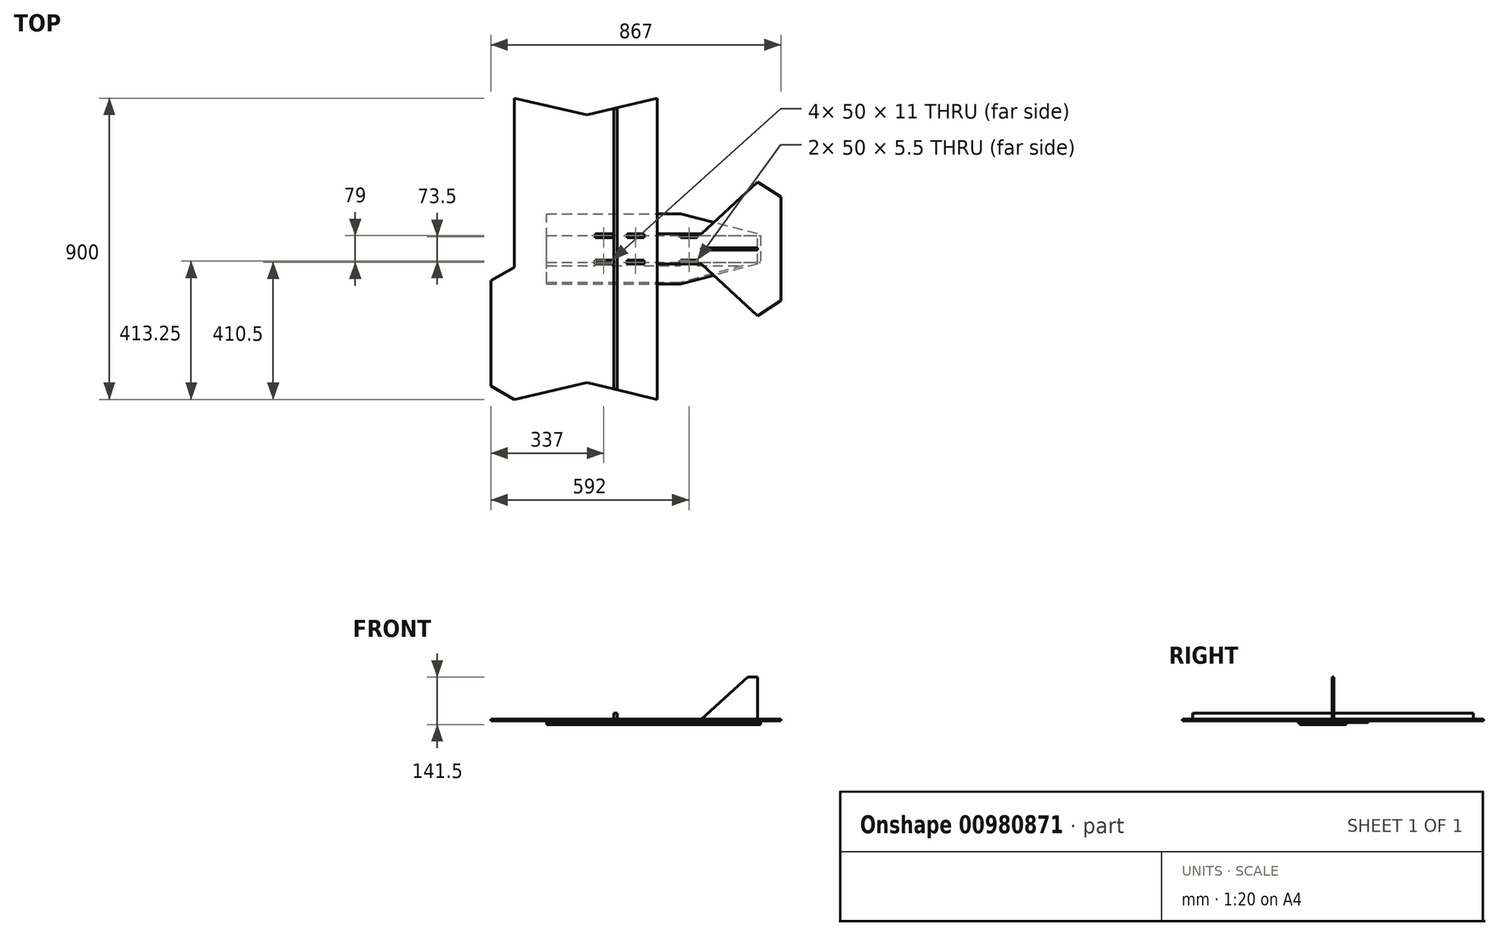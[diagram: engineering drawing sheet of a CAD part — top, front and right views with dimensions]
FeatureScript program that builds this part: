
annotation { "Feature Type Name" : "Feature", "Feature Type Description" : "" }
export const myFeature = defineFeature(function(context is Context, id is Id, definition is map)
    precondition{}
    {
        {
            var Q0;
            Q0=qCreatedBy(makeId("Top.planeOp"),FACE);
            var sketch = newSketch(context, id + "F0", { "sketchPlane" : qUnion([Q0])});
            skPoint(sketch, "E0.middle", {"position": v(0, 0) * mm});
            skLineSegment(sketch, "E1.bottom", {"start": v(0, 0) * mm, "end": v(-287, 0) * mm, "construction": true});
            skLineSegment(sketch, "E1.left", {"start": v(0, 0) * mm, "end": v(0, 400) * mm});
            skLineSegment(sketch, "E2.MirrorCS", {"start": v(0, 0) * mm, "end": v(0, -400) * mm});
            skLineSegment(sketch, "E3.bottom", {"start": v(0, 0) * mm, "end": v(210, 0) * mm, "construction": true});
            skLineSegment(sketch, "E3.right", {"start": v(210, 0) * mm, "end": v(210, 450) * mm});
            skLineSegment(sketch, "E4.MirrorCS", {"start": v(210, 0) * mm, "end": v(210, -450) * mm});
            skLineSegment(sketch, "E5", {"start": v(-217, 450) * mm, "end": v(-217, 55) * mm});
            skLineSegment(sketch, "E6", {"start": v(0, 400) * mm, "end": v(210, 450) * mm});
            skLineSegment(sketch, "E7", {"start": v(-217, 450) * mm, "end": v(-217, 400) * mm});
            skLineSegment(sketch, "E8", {"start": v(-217, 450) * mm, "end": v(0, 400) * mm});
            skLineSegment(sketch, "E9.MirrorCS", {"start": v(-217, -450) * mm, "end": v(0, -400) * mm});
            skLineSegment(sketch, "E10.MirrorCS", {"start": v(0, -400) * mm, "end": v(210, -450) * mm});
            skLineSegment(sketch, "E11", {"start": v(210, 45) * mm, "end": v(-287, 45) * mm, "construction": true});
            skLineSegment(sketch, "E12.MirrorCS", {"start": v(25, 45) * mm, "end": v(25, 34) * mm});
            skLineSegment(sketch, "E13.MirrorCS", {"start": v(75, 45) * mm, "end": v(75, 34) * mm});
            skLineSegment(sketch, "E14.MirrorCS", {"start": v(170, 45) * mm, "end": v(170, 34) * mm});
            skLineSegment(sketch, "E15.MirrorCS", {"start": v(120, 45) * mm, "end": v(120, 34) * mm});
            skLineSegment(sketch, "E16.MirrorCS", {"start": v(25, 45) * mm, "end": v(75, 45) * mm});
            skLineSegment(sketch, "E17.MirrorCS", {"start": v(120, 34) * mm, "end": v(170, 34) * mm});
            skLineSegment(sketch, "E18.MirrorCS", {"start": v(25, 34) * mm, "end": v(75, 34) * mm});
            skLineSegment(sketch, "E19.MirrorCS", {"start": v(120, 45) * mm, "end": v(170, 45) * mm});
            skLineSegment(sketch, "E20.MirrorCS", {"start": v(120, -45) * mm, "end": v(120, -34) * mm});
            skLineSegment(sketch, "E21.MirrorCS", {"start": v(75, -45) * mm, "end": v(75, -34) * mm});
            skLineSegment(sketch, "E22.MirrorCS", {"start": v(25, -45) * mm, "end": v(25, -34) * mm});
            skLineSegment(sketch, "E23.MirrorCS", {"start": v(170, -45) * mm, "end": v(170, -34) * mm});
            skLineSegment(sketch, "E24.MirrorCS", {"start": v(25, -45) * mm, "end": v(75, -45) * mm});
            skLineSegment(sketch, "E25.MirrorCS", {"start": v(120, -45) * mm, "end": v(170, -45) * mm});
            skLineSegment(sketch, "E26.MirrorCS", {"start": v(210, -45) * mm, "end": v(-287, -45) * mm, "construction": true});
            skLineSegment(sketch, "E27.MirrorCS", {"start": v(120, -34) * mm, "end": v(170, -34) * mm});
            skLineSegment(sketch, "E28.MirrorCS", {"start": v(25, -34) * mm, "end": v(75, -34) * mm});
            skLineSegment(sketch, "E29", {"start": v(80, 450) * mm, "end": v(80, -450) * mm, "construction": true});
            skLineSegment(sketch, "E30.bottom", {"start": v(80, 115) * mm, "end": v(91, 115) * mm});
            skLineSegment(sketch, "E30.top", {"start": v(80, 165) * mm, "end": v(91, 165) * mm});
            skLineSegment(sketch, "E30.left", {"start": v(80, 115) * mm, "end": v(80, 165) * mm});
            skLineSegment(sketch, "E30.right", {"start": v(91, 115) * mm, "end": v(91, 165) * mm});
            skLineSegment(sketch, "E31.bottom", {"start": v(80, 275) * mm, "end": v(91, 275) * mm});
            skLineSegment(sketch, "E31.top", {"start": v(80, 325) * mm, "end": v(91, 325) * mm});
            skLineSegment(sketch, "E31.left", {"start": v(80, 275) * mm, "end": v(80, 325) * mm});
            skLineSegment(sketch, "E31.right", {"start": v(91, 275) * mm, "end": v(91, 325) * mm});
            skLineSegment(sketch, "E32.MirrorCS", {"start": v(80, -275) * mm, "end": v(80, -325) * mm});
            skLineSegment(sketch, "E33.MirrorCS", {"start": v(80, -115) * mm, "end": v(80, -165) * mm});
            skLineSegment(sketch, "E34.MirrorCS", {"start": v(91, -115) * mm, "end": v(91, -165) * mm});
            skLineSegment(sketch, "E35.MirrorCS", {"start": v(91, -275) * mm, "end": v(91, -325) * mm});
            skLineSegment(sketch, "E36.MirrorCS", {"start": v(80, -165) * mm, "end": v(91, -165) * mm});
            skLineSegment(sketch, "E37.MirrorCS", {"start": v(80, -325) * mm, "end": v(91, -325) * mm});
            skLineSegment(sketch, "E38.MirrorCS", {"start": v(80, -450) * mm, "end": v(80, 419.05) * mm, "construction": true});
            skLineSegment(sketch, "E39.MirrorCS", {"start": v(80, -115) * mm, "end": v(91, -115) * mm});
            skLineSegment(sketch, "E40.MirrorCS", {"start": v(80, -275) * mm, "end": v(91, -275) * mm});
            skLineSegment(sketch, "E41", {"start": v(-217, -450) * mm, "end": v(-287, -410) * mm});
            skLineSegment(sketch, "E42.MirrorCS", {"start": v(-217, 450) * mm, "end": v(-287, 410) * mm});
            skLineSegment(sketch, "E43", {"start": v(-287, -85) * mm, "end": v(-287, -85) * mm});
            skLineSegment(sketch, "E44", {"start": v(-287, 95) * mm, "end": v(-287, 410) * mm});
            skPoint(sketch, "E45.orphan", {"position": v(-287, -450) * mm});
            skLineSegment(sketch, "E46.trimOffspring", {"start": v(-287, -95) * mm, "end": v(-287, -410) * mm});
            skPoint(sketch, "E47.MirrorCS.start.orphan", {"position": v(-287, 0) * mm});
            skPoint(sketch, "E48.end.orphan", {"position": v(-287, 450) * mm});
            skPoint(sketch, "E49.orphan", {"position": v(0, 450) * mm});
            skPoint(sketch, "E50.orphan", {"position": v(80, 450) * mm});
            skPoint(sketch, "E51.MirrorCS.start.orphan", {"position": v(0, -450) * mm});
            skPoint(sketch, "E52.MirrorCS.end.orphan", {"position": v(210, -450) * mm});
            skLineSegment(sketch, "E53", {"start": v(-217, 55) * mm, "end": v(-144.76, 55) * mm, "construction": true});
            skLineSegment(sketch, "E54", {"start": v(-287, 95) * mm, "end": v(-242.26, 95) * mm, "construction": true});
            skLineSegment(sketch, "E55", {"start": v(-287, 95) * mm, "end": v(-217, 55) * mm});
            skPoint(sketch, "E56.MirrorCS.end.orphan", {"position": v(-287, 85) * mm});
            skLineSegment(sketch, "E57.MirrorCS", {"start": v(-287, -95) * mm, "end": v(-217, -55) * mm});
            skLineSegment(sketch, "E58.trimOffspring", {"start": v(-217, -55) * mm, "end": v(-217, -450) * mm});
            skPoint(sketch, "E59.trimOffspring.end.orphan", {"position": v(-217, -45) * mm});
            skPoint(sketch, "E60.start.orphan", {"position": v(-217, 45) * mm});
            skLineSegment(sketch, "E61", {"start": v(-217, 55) * mm, "end": v(-217, -55) * mm});
            skSolve(sketch);
        }
        {
            var Q0;
            {var subQ4=sQuery(id+"F0.wireOp",EDGE,"E1.left");Q0=makeQuery(id+"F0.imprint","IMPRINT",FACE,{"disambiguationData":[TD([[makeQuery(id+"F0.imprint","IMPRINT",EDGE,{"derivedFrom":subQ4}),1.0]])]});}
            var Q1;
            {var subQ1=sQuery(id+"F0.wireOp",EDGE,"E7");Q1=makeQuery(id+"F0.imprint","IMPRINT",FACE,{"disambiguationData":[TD([[makeQuery(id+"F0.imprint","IMPRINT",EDGE,{"derivedFrom":subQ1}),-1.0]])]});}
            var Q2;
            {var subQ0=sQuery(id+"F0.wireOp",EDGE,"lml2tlPo-69tN-Frwz-FPkp-IQI1zHHmHSO9");Q2=makeQuery(id+"F0.imprint","IMPRINT",FACE,{"disambiguationData":[TD([[makeQuery(id+"F0.imprint","IMPRINT",EDGE,{"derivedFrom":subQ0}),1.0]])]});}
            var Q3;
            {var subQ1=sQuery(id+"F0.wireOp",EDGE,"E1.left");Q3=makeQuery(id+"F0.imprint","IMPRINT",FACE,{"disambiguationData":[TD([[makeQuery(id+"F0.imprint","IMPRINT",EDGE,{"derivedFrom":subQ1}),-1.0]])]});}
            var Q4;
            Q4=makeQuery(id+"F0.imprint","IMPRINT",FACE,{"disambiguationData":[TD([[makeQuery(id+"F0.imprint","IMPRINT",EDGE,{"derivedFrom":sQuery(id+"F0.wireOp",EDGE,"E41")}),-1.0]])]});
            extrude(context, id + "F1", {"entities" : qUnion([Q0, Q1, Q2, Q3, Q4]), "depth" : 5.5 * mm, "offsetDistance" : 25 * mm});
        }
        {
            var Q0;
            Q0=makeQuery(id+"F1.opExtrude","CAP_FACE",FACE,{"disambiguationData":[OSD([sQuery(id+"F0.wireOp",EDGE,"E1.right"),sQuery(id+"F0.wireOp",EDGE,"E47.MirrorCS"),sQuery(id+"F0.wireOp",EDGE,"E3.right"),sQuery(id+"F0.wireOp",EDGE,"E4.MirrorCS"),sQuery(id+"F0.wireOp",EDGE,"E5"),sQuery(id+"F0.wireOp",EDGE,"E6"),sQuery(id+"F0.wireOp",EDGE,"E8"),sQuery(id+"F0.wireOp",EDGE,"E9.MirrorCS"),sQuery(id+"F0.wireOp",EDGE,"E10.MirrorCS"),sQuery(id+"F0.wireOp",EDGE,"E12.MirrorCS"),sQuery(id+"F0.wireOp",EDGE,"E13.MirrorCS"),sQuery(id+"F0.wireOp",EDGE,"E14.MirrorCS"),sQuery(id+"F0.wireOp",EDGE,"E15.MirrorCS"),sQuery(id+"F0.wireOp",EDGE,"E16.MirrorCS"),sQuery(id+"F0.wireOp",EDGE,"E17.MirrorCS"),sQuery(id+"F0.wireOp",EDGE,"E18.MirrorCS"),sQuery(id+"F0.wireOp",EDGE,"E19.MirrorCS"),sQuery(id+"F0.wireOp",EDGE,"E20.MirrorCS"),sQuery(id+"F0.wireOp",EDGE,"E21.MirrorCS"),sQuery(id+"F0.wireOp",EDGE,"E22.MirrorCS"),sQuery(id+"F0.wireOp",EDGE,"E23.MirrorCS"),sQuery(id+"F0.wireOp",EDGE,"E24.MirrorCS"),sQuery(id+"F0.wireOp",EDGE,"E25.MirrorCS"),sQuery(id+"F0.wireOp",EDGE,"E27.MirrorCS"),sQuery(id+"F0.wireOp",EDGE,"E28.MirrorCS"),sQuery(id+"F0.wireOp",EDGE,"E30.bottom"),sQuery(id+"F0.wireOp",EDGE,"E30.top"),sQuery(id+"F0.wireOp",EDGE,"E30.left"),sQuery(id+"F0.wireOp",EDGE,"E30.right"),sQuery(id+"F0.wireOp",EDGE,"E31.bottom"),sQuery(id+"F0.wireOp",EDGE,"E31.top"),sQuery(id+"F0.wireOp",EDGE,"E31.left"),sQuery(id+"F0.wireOp",EDGE,"E31.right"),sQuery(id+"F0.wireOp",EDGE,"E32.MirrorCS"),sQuery(id+"F0.wireOp",EDGE,"E33.MirrorCS"),sQuery(id+"F0.wireOp",EDGE,"E34.MirrorCS"),sQuery(id+"F0.wireOp",EDGE,"E35.MirrorCS"),sQuery(id+"F0.wireOp",EDGE,"E36.MirrorCS"),sQuery(id+"F0.wireOp",EDGE,"E37.MirrorCS"),sQuery(id+"F0.wireOp",EDGE,"E39.MirrorCS"),sQuery(id+"F0.wireOp",EDGE,"E40.MirrorCS"),sQuery(id+"F0.wireOp",EDGE,"lml2tlPo-69tN-Frwz-FPkp-IQI1zHHmHSO9"),sQuery(id+"F0.wireOp",EDGE,"E41"),sQuery(id+"F0.wireOp",EDGE,"E56.MirrorCS"),sQuery(id+"F0.wireOp",EDGE,"E42.MirrorCS")])],"isStart":false});
            var sketch = newSketch(context, id + "F2", { "sketchPlane" : qUnion([Q0])});
            skLineSegment(sketch, "E62.0", {"start": v(80, -450) * mm, "end": v(80, 419.05) * mm});
            skLineSegment(sketch, "E63.0", {"start": v(91, -275) * mm, "end": v(91, -325) * mm});
            skLineSegment(sketch, "E63.1", {"start": v(80, -275) * mm, "end": v(80, -325) * mm});
            skLineSegment(sketch, "E63.2", {"start": v(80, -115) * mm, "end": v(80, -165) * mm});
            skLineSegment(sketch, "E63.3", {"start": v(91, -115) * mm, "end": v(91, -165) * mm});
            skLineSegment(sketch, "E64.0", {"start": v(91, 115) * mm, "end": v(91, 165) * mm});
            skLineSegment(sketch, "E64.1", {"start": v(80, 115) * mm, "end": v(80, 165) * mm});
            skLineSegment(sketch, "E64.2", {"start": v(80, 275) * mm, "end": v(80, 325) * mm});
            skLineSegment(sketch, "E64.3", {"start": v(91, 275) * mm, "end": v(91, 325) * mm});
            skPoint(sketch, "E65.0", {"position": v(105, 425) * mm});
            skLineSegment(sketch, "E66.0", {"start": v(0, -400) * mm, "end": v(210, -450) * mm});
            skLineSegment(sketch, "E67.0", {"start": v(0, 400) * mm, "end": v(210, 450) * mm});
            skLineSegment(sketch, "E68", {"start": v(80, 419.05) * mm, "end": v(91, 419.05) * mm});
            skLineSegment(sketch, "E69.bottom", {"start": v(80, -419.05) * mm, "end": v(91, -419.05) * mm});
            skLineSegment(sketch, "E69.left", {"start": v(80, -419.05) * mm, "end": v(80, 419.05) * mm});
            skLineSegment(sketch, "E69.right", {"start": v(91, -419.05) * mm, "end": v(91, 419.05) * mm});
            skSolve(sketch);
        }
        {
            var Q0;
            {var subQ0=sQuery(id+"F2.wireOp",EDGE,"E69.bottom");Q0=makeQuery(id+"F2.imprint","IMPRINT",FACE,{"disambiguationData":[TD([[makeQuery(id+"F2.imprint","IMPRINT",EDGE,{"derivedFrom":subQ0}),1.0]])]});}
            var Q1;
            {var subQ2=makeQuery(id+"F1.opExtrude","CAP_EDGE",EDGE,{"disambiguationData":[OSD([sQuery(id+"F0.wireOp",EDGE,"E37.MirrorCS")])],"isStart":false});Q1=makeQuery(id+"F2.imprint","IMPRINT",FACE,{"disambiguationData":[TD([[makeQuery(id+"F2.imprint","IMPRINT",EDGE,{"derivedFrom":subQ2}),1.0]])]});}
            var Q2;
            {var subQ2=makeQuery(id+"F1.opExtrude","CAP_EDGE",EDGE,{"disambiguationData":[OSD([sQuery(id+"F0.wireOp",EDGE,"E36.MirrorCS")])],"isStart":false});Q2=makeQuery(id+"F2.imprint","IMPRINT",FACE,{"disambiguationData":[TD([[makeQuery(id+"F2.imprint","IMPRINT",EDGE,{"derivedFrom":subQ2}),-1.0]])]});}
            var Q3;
            {var subQ2=makeQuery(id+"F1.opExtrude","CAP_EDGE",EDGE,{"disambiguationData":[OSD([sQuery(id+"F0.wireOp",EDGE,"E36.MirrorCS")])],"isStart":false});Q3=makeQuery(id+"F2.imprint","IMPRINT",FACE,{"disambiguationData":[TD([[makeQuery(id+"F2.imprint","IMPRINT",EDGE,{"derivedFrom":subQ2}),1.0]])]});}
            var Q4;
            {var subQ1=makeQuery(id+"F1.opExtrude","CAP_EDGE",EDGE,{"disambiguationData":[OSD([sQuery(id+"F0.wireOp",EDGE,"E30.bottom")])],"isStart":false});Q4=makeQuery(id+"F2.imprint","IMPRINT",FACE,{"disambiguationData":[TD([[makeQuery(id+"F2.imprint","IMPRINT",EDGE,{"derivedFrom":subQ1}),-1.0]])]});}
            var Q5;
            {var subQ1=makeQuery(id+"F1.opExtrude","CAP_EDGE",EDGE,{"disambiguationData":[OSD([sQuery(id+"F0.wireOp",EDGE,"E30.bottom")])],"isStart":false});Q5=makeQuery(id+"F2.imprint","IMPRINT",FACE,{"disambiguationData":[TD([[makeQuery(id+"F2.imprint","IMPRINT",EDGE,{"derivedFrom":subQ1}),1.0]])]});}
            var Q6;
            {var subQ1=makeQuery(id+"F1.opExtrude","CAP_EDGE",EDGE,{"disambiguationData":[OSD([sQuery(id+"F0.wireOp",EDGE,"E30.top")])],"isStart":false});Q6=makeQuery(id+"F2.imprint","IMPRINT",FACE,{"disambiguationData":[TD([[makeQuery(id+"F2.imprint","IMPRINT",EDGE,{"derivedFrom":subQ1}),1.0]])]});}
            var Q7;
            {var subQ0=sQuery(id+"F2.wireOp",EDGE,"E68");Q7=makeQuery(id+"F2.imprint","IMPRINT",FACE,{"disambiguationData":[TD([[makeQuery(id+"F2.imprint","IMPRINT",EDGE,{"derivedFrom":subQ0}),-1.0]])]});}
            var Q8;
            {var subQ1=makeQuery(id+"F1.opExtrude","CAP_EDGE",EDGE,{"disambiguationData":[OSD([sQuery(id+"F0.wireOp",EDGE,"E31.bottom")])],"isStart":false});Q8=makeQuery(id+"F2.imprint","IMPRINT",FACE,{"disambiguationData":[TD([[makeQuery(id+"F2.imprint","IMPRINT",EDGE,{"derivedFrom":subQ1}),1.0]])]});}
            extrude(context, id + "F3", {"entities" : qUnion([Q0, Q1, Q2, Q3, Q4, Q5, Q6, Q7, Q8]), "depth" : 18 * mm, "offsetDistance" : 25 * mm});
        }
        {
            var Q0;
            Q0=makeQuery(id+"F0.imprint","IMPRINT",FACE,{"disambiguationData":[TD([[makeQuery(id+"F0.imprint","IMPRINT",EDGE,{"derivedFrom":sQuery(id+"F0.wireOp",EDGE,"E32.MirrorCS")}),1.0]])]});
            var Q1;
            Q1=makeQuery(id+"F0.imprint","IMPRINT",FACE,{"disambiguationData":[TD([[makeQuery(id+"F0.imprint","IMPRINT",EDGE,{"derivedFrom":sQuery(id+"F0.wireOp",EDGE,"E33.MirrorCS")}),1.0]])]});
            var Q2;
            Q2=makeQuery(id+"F0.imprint","IMPRINT",FACE,{"disambiguationData":[TD([[makeQuery(id+"F0.imprint","IMPRINT",EDGE,{"derivedFrom":sQuery(id+"F0.wireOp",EDGE,"E30.bottom")}),1.0]])]});
            var Q3;
            Q3=makeQuery(id+"F0.imprint","IMPRINT",FACE,{"disambiguationData":[TD([[makeQuery(id+"F0.imprint","IMPRINT",EDGE,{"derivedFrom":sQuery(id+"F0.wireOp",EDGE,"E31.bottom")}),1.0]])]});
            extrude(context, id + "F4", {"entities" : qUnion([Q0, Q1, Q2, Q3]), "operationType" : NewBodyOperationType.ADD, "depth" : 5.5 * mm, "offsetDistance" : 25 * mm});
        }
        {
            var Q0;
            {var subQ4=sQuery(id+"F0.wireOp",EDGE,"E1.left");Q0=makeQuery(id+"F0.imprint","IMPRINT",FACE,{"disambiguationData":[TD([[makeQuery(id+"F0.imprint","IMPRINT",EDGE,{"derivedFrom":subQ4}),1.0]])]});}
            var sketch = newSketch(context, id + "F5", { "sketchPlane" : qUnion([Q0])});
            skLineSegment(sketch, "E70.2", {"start": v(120, 34) * mm, "end": v(170, 34) * mm});
            skLineSegment(sketch, "E70.4", {"start": v(120, -34) * mm, "end": v(170, -34) * mm});
            skLineSegment(sketch, "E70.6", {"start": v(25, 34) * mm, "end": v(75, 34) * mm});
            skLineSegment(sketch, "E70.8", {"start": v(25, -34) * mm, "end": v(75, -34) * mm});
            skLineSegment(sketch, "E71.0", {"start": v(210, 45) * mm, "end": v(170, 45) * mm});
            skLineSegment(sketch, "E72", {"start": v(-120, 45) * mm, "end": v(-120, -45) * mm});
            skLineSegment(sketch, "E73", {"start": v(-120, -45) * mm, "end": v(-120, -105) * mm});
            skLineSegment(sketch, "E74", {"start": v(-120, -105) * mm, "end": v(280, -105) * mm});
            skLineSegment(sketch, "E75", {"start": v(510, -45) * mm, "end": v(510, 0) * mm});
            skLineSegment(sketch, "E76", {"start": v(210, -45) * mm, "end": v(510, -45) * mm});
            skLineSegment(sketch, "E77", {"start": v(510, -45) * mm, "end": v(280, -105) * mm});
            skLineSegment(sketch, "E78.MirrorCS", {"start": v(210, 45) * mm, "end": v(510, 45) * mm});
            skLineSegment(sketch, "E79.MirrorCS", {"start": v(510, 45) * mm, "end": v(510, 0) * mm});
            skLineSegment(sketch, "E80.MirrorCS", {"start": v(510, 45) * mm, "end": v(280, 105) * mm});
            skLineSegment(sketch, "E81.MirrorCS", {"start": v(-120, 105) * mm, "end": v(280, 105) * mm});
            skLineSegment(sketch, "E82.MirrorCS", {"start": v(-120, 45) * mm, "end": v(-120, 105) * mm});
            skPoint(sketch, "E70.1.end.orphan", {"position": v(210, 0) * mm});
            skPoint(sketch, "E70.5.end.orphan", {"position": v(75, 45) * mm});
            skPoint(sketch, "E70.5.start.orphan", {"position": v(25, 45) * mm});
            skLineSegment(sketch, "E83.trimOffspring", {"start": v(25, 45) * mm, "end": v(-120, 45) * mm});
            skPoint(sketch, "E70.3.end.orphan", {"position": v(170, 45) * mm});
            skPoint(sketch, "E70.3.start.orphan", {"position": v(120, 45) * mm});
            skLineSegment(sketch, "E84.trimOffspring", {"start": v(120, 45) * mm, "end": v(75, 45) * mm});
            skPoint(sketch, "E70.0.end.orphan", {"position": v(75, -45) * mm});
            skPoint(sketch, "E70.0.start.orphan", {"position": v(25, -45) * mm});
            skLineSegment(sketch, "E85.trimOffspring", {"start": v(120, -45) * mm, "end": v(75, -45) * mm});
            skPoint(sketch, "E70.7.end.orphan", {"position": v(170, -45) * mm});
            skLineSegment(sketch, "E86.trimOffspring", {"start": v(25, -45) * mm, "end": v(-120, -45) * mm});
            skLineSegment(sketch, "E87", {"start": v(210, -45) * mm, "end": v(170, -45) * mm});
            skLineSegment(sketch, "E88", {"start": v(170, 45) * mm, "end": v(170, 34) * mm});
            skLineSegment(sketch, "E89", {"start": v(120, 34) * mm, "end": v(120, 45) * mm});
            skLineSegment(sketch, "E90", {"start": v(120, -34) * mm, "end": v(120, -45) * mm});
            skLineSegment(sketch, "E91", {"start": v(170, -34) * mm, "end": v(170, -45) * mm});
            skLineSegment(sketch, "E92", {"start": v(75, 34) * mm, "end": v(75, 45) * mm});
            skLineSegment(sketch, "E93", {"start": v(75, -34) * mm, "end": v(75, -45) * mm});
            skLineSegment(sketch, "E94", {"start": v(25, 34) * mm, "end": v(25, 45) * mm});
            skLineSegment(sketch, "E95", {"start": v(25, -34) * mm, "end": v(25, -45) * mm});
            skPoint(sketch, "E96.orphan", {"position": v(0, 0) * mm});
            skPoint(sketch, "E97.orphan", {"position": v(-287, -45) * mm});
            skPoint(sketch, "E98.orphan", {"position": v(-287, 45) * mm});
            skPoint(sketch, "E99.orphan", {"position": v(0, -400) * mm});
            skPoint(sketch, "E100.trimOffspring.end.orphan", {"position": v(210, -450) * mm});
            skPoint(sketch, "E101.trimOffspring.end.orphan", {"position": v(210, 450) * mm});
            skPoint(sketch, "E102.orphan", {"position": v(0, 400) * mm});
            skLineSegment(sketch, "E103", {"start": v(280, -45) * mm, "end": v(280, -39.5) * mm, "construction": true});
            skLineSegment(sketch, "E104", {"start": v(280, -39.5) * mm, "end": v(280, -34) * mm});
            skLineSegment(sketch, "E105", {"start": v(280, -34) * mm, "end": v(330, -34) * mm});
            skLineSegment(sketch, "E106", {"start": v(330, -34) * mm, "end": v(330, -39.5) * mm});
            skLineSegment(sketch, "E107", {"start": v(330, -39.5) * mm, "end": v(330, -45) * mm, "construction": true});
            skLineSegment(sketch, "E108", {"start": v(280, -39.5) * mm, "end": v(330, -39.5) * mm});
            skLineSegment(sketch, "E109", {"start": v(210, 0) * mm, "end": v(384.7, 0) * mm, "construction": true});
            skLineSegment(sketch, "E110.MirrorCS", {"start": v(280, 39.5) * mm, "end": v(280, 34) * mm});
            skLineSegment(sketch, "E111.MirrorCS", {"start": v(280, 34) * mm, "end": v(330, 34) * mm});
            skLineSegment(sketch, "E112.MirrorCS", {"start": v(280, 39.5) * mm, "end": v(330, 39.5) * mm});
            skLineSegment(sketch, "E113.MirrorCS", {"start": v(330, 34) * mm, "end": v(330, 39.5) * mm});
            skSolve(sketch);
        }
        {
            var Q0;
            Q0=makeQuery(id+"F5.imprint","IMPRINT",FACE,{"disambiguationData":[TD([[makeQuery(id+"F5.imprint","IMPRINT",EDGE,{"derivedFrom":sQuery(id+"F5.wireOp",EDGE,"E70.4")}),-1.0]])]});
            var Q1;
            Q1=makeQuery(id+"F5.imprint","IMPRINT",FACE,{"disambiguationData":[TD([[makeQuery(id+"F5.imprint","IMPRINT",EDGE,{"derivedFrom":sQuery(id+"F5.wireOp",EDGE,"E70.2")}),-1.0]])]});
            var Q2;
            Q2=makeQuery(id+"F5.imprint","IMPRINT",FACE,{"disambiguationData":[TD([[makeQuery(id+"F5.imprint","IMPRINT",EDGE,{"derivedFrom":sQuery(id+"F5.wireOp",EDGE,"E70.2")}),1.0]])]});
            var Q3;
            {var subQ0=sQuery(id+"F5.wireOp",EDGE,"E82.MirrorCS");Q3=makeQuery(id+"F5.imprint","IMPRINT",FACE,{"disambiguationData":[TD([[makeQuery(id+"F5.imprint","IMPRINT",EDGE,{"derivedFrom":subQ0}),-1.0]])]});}
            var Q4;
            {var subQ1=sQuery(id+"F5.wireOp",EDGE,"E72");Q4=makeQuery(id+"F5.imprint","IMPRINT",FACE,{"disambiguationData":[TD([[makeQuery(id+"F5.imprint","IMPRINT",EDGE,{"derivedFrom":subQ1}),1.0]])]});}
            var Q5;
            {var subQ0=sQuery(id+"F5.wireOp",EDGE,"E73");Q5=makeQuery(id+"F5.imprint","IMPRINT",FACE,{"disambiguationData":[TD([[makeQuery(id+"F5.imprint","IMPRINT",EDGE,{"derivedFrom":subQ0}),1.0]])]});}
            extrude(context, id + "F6", {"entities" : qUnion([Q0, Q1, Q2, Q3, Q4, Q5]), "oppositeDirection" : true, "depth" : 5.5 * mm, "offsetDistance" : 25 * mm});
        }
        {
            var Q0;
            Q0=makeQuery(id+"F6.opExtrude","CAP_FACE",FACE,{"disambiguationData":[OSD([sQuery(id+"F5.wireOp",EDGE,"E72"),sQuery(id+"F5.wireOp",EDGE,"E73"),sQuery(id+"F5.wireOp",EDGE,"E74"),sQuery(id+"F5.wireOp",EDGE,"E75"),sQuery(id+"F5.wireOp",EDGE,"E77"),sQuery(id+"F5.wireOp",EDGE,"E79.MirrorCS"),sQuery(id+"F5.wireOp",EDGE,"E80.MirrorCS"),sQuery(id+"F5.wireOp",EDGE,"E81.MirrorCS"),sQuery(id+"F5.wireOp",EDGE,"E82.MirrorCS")])],"isStart":false});
            var sketch = newSketch(context, id + "F7", { "sketchPlane" : qUnion([Q0])});
            skLineSegment(sketch, "E114.0", {"start": v(120, 45) * mm, "end": v(75, 45) * mm, "construction": true});
            skLineSegment(sketch, "E114.1", {"start": v(25, 45) * mm, "end": v(-120, 45) * mm, "construction": true});
            skLineSegment(sketch, "E114.2", {"start": v(-120, -105) * mm, "end": v(280, -105) * mm, "construction": true});
            skLineSegment(sketch, "E114.3", {"start": v(510, 45) * mm, "end": v(510, 0) * mm, "construction": true});
            skLineSegment(sketch, "E114.5", {"start": v(-120, 105) * mm, "end": v(280, 105) * mm, "construction": true});
            skLineSegment(sketch, "E114.6", {"start": v(510, -45) * mm, "end": v(510, 0) * mm, "construction": true});
            skLineSegment(sketch, "E114.7", {"start": v(-120, -45) * mm, "end": v(-120, -105) * mm, "construction": true});
            skLineSegment(sketch, "E114.8", {"start": v(510, -45) * mm, "end": v(280, -105) * mm, "construction": true});
            skLineSegment(sketch, "E114.10", {"start": v(210, -45) * mm, "end": v(170, -45) * mm, "construction": true});
            skLineSegment(sketch, "E114.11", {"start": v(210, 45) * mm, "end": v(170, 45) * mm, "construction": true});
            skLineSegment(sketch, "E114.12", {"start": v(-120, -45) * mm, "end": v(-120, 45) * mm, "construction": true});
            skLineSegment(sketch, "E114.13", {"start": v(25, -45) * mm, "end": v(-120, -45) * mm, "construction": true});
            skLineSegment(sketch, "E114.14", {"start": v(210, -45) * mm, "end": v(510, -45) * mm, "construction": true});
            skLineSegment(sketch, "E114.15", {"start": v(510, 45) * mm, "end": v(280, 105) * mm, "construction": true});
            skLineSegment(sketch, "E114.16", {"start": v(210, 45) * mm, "end": v(510, 45) * mm, "construction": true});
            skLineSegment(sketch, "E114.17", {"start": v(120, -45) * mm, "end": v(75, -45) * mm, "construction": true});
            skLineSegment(sketch, "E114.20", {"start": v(-120, 45) * mm, "end": v(-120, 105) * mm});
            skLineSegment(sketch, "E115.0", {"start": v(508.61, -39.68) * mm, "end": v(279.3, -99.5) * mm, "construction": true});
            skLineSegment(sketch, "E115.1", {"start": v(-120, -99.5) * mm, "end": v(279.3, -99.5) * mm, "construction": true});
            skLineSegment(sketch, "E116", {"start": v(-120, -45) * mm, "end": v(510, -45) * mm, "construction": true});
            skLineSegment(sketch, "E117.0", {"start": v(-120, -50.5) * mm, "end": v(510, -50.5) * mm, "construction": true});
            skLineSegment(sketch, "E118", {"start": v(-120, -50.5) * mm, "end": v(25, -50.5) * mm});
            skLineSegment(sketch, "E119", {"start": v(25, -50.5) * mm, "end": v(25, -39.5) * mm});
            skLineSegment(sketch, "E120", {"start": v(75, -39.5) * mm, "end": v(75, -50.5) * mm});
            skLineSegment(sketch, "E121", {"start": v(75, -50.5) * mm, "end": v(120, -50.5) * mm});
            skLineSegment(sketch, "E122", {"start": v(120, -50.5) * mm, "end": v(120, -39.5) * mm});
            skLineSegment(sketch, "E123", {"start": v(170, -39.5) * mm, "end": v(170, -50.5) * mm});
            skLineSegment(sketch, "E124", {"start": v(170, -50.5) * mm, "end": v(467.13, -50.5) * mm});
            skLineSegment(sketch, "E125", {"start": v(467.13, -50.5) * mm, "end": v(279.3, -99.5) * mm});
            skLineSegment(sketch, "E126", {"start": v(279.3, -99.5) * mm, "end": v(-120, -99.5) * mm});
            skLineSegment(sketch, "E127", {"start": v(-120, -99.5) * mm, "end": v(-120, -50.5) * mm});
            skLineSegment(sketch, "E128", {"start": v(510, 0) * mm, "end": v(-120, 0) * mm, "construction": true});
            skLineSegment(sketch, "E129.MirrorCS", {"start": v(170, 39.5) * mm, "end": v(170, 50.5) * mm});
            skLineSegment(sketch, "E130.MirrorCS", {"start": v(120, 50.5) * mm, "end": v(120, 39.5) * mm});
            skLineSegment(sketch, "E131.MirrorCS", {"start": v(-120, 99.5) * mm, "end": v(279.3, 99.5) * mm});
            skLineSegment(sketch, "E132.MirrorCS", {"start": v(-120, 50.5) * mm, "end": v(-120, 99.5) * mm, "construction": true});
            skLineSegment(sketch, "E133.MirrorCS", {"start": v(75, 39.5) * mm, "end": v(75, 50.5) * mm});
            skLineSegment(sketch, "E134.MirrorCS", {"start": v(25, 50.5) * mm, "end": v(25, 39.5) * mm});
            skLineSegment(sketch, "E135.MirrorCS", {"start": v(-120, 50.5) * mm, "end": v(25, 50.5) * mm});
            skLineSegment(sketch, "E136.trimOffspring", {"start": v(467.13, 50.5) * mm, "end": v(279.3, 99.5) * mm});
            skPoint(sketch, "E137.trimOffspring.end.orphan", {"position": v(510, 50.5) * mm});
            skPoint(sketch, "E138.MirrorCS.start.orphan", {"position": v(508.61, 39.68) * mm});
            skPoint(sketch, "E114.9.end.orphan", {"position": v(170, 34) * mm});
            skPoint(sketch, "E114.9.start.orphan", {"position": v(120, 34) * mm});
            skPoint(sketch, "E114.18.end.orphan", {"position": v(75, 34) * mm});
            skPoint(sketch, "E114.18.start.orphan", {"position": v(25, 34) * mm});
            skPoint(sketch, "E114.19.end.orphan", {"position": v(75, -34) * mm});
            skPoint(sketch, "E114.19.start.orphan", {"position": v(25, -34) * mm});
            skPoint(sketch, "E114.4.end.orphan", {"position": v(170, -34) * mm});
            skPoint(sketch, "E114.4.start.orphan", {"position": v(120, -34) * mm});
            skLineSegment(sketch, "E139.trimOffspring", {"start": v(170, 50.5) * mm, "end": v(280, 50.5) * mm});
            skLineSegment(sketch, "E140.trimOffspring", {"start": v(75, 50.5) * mm, "end": v(120, 50.5) * mm});
            skPoint(sketch, "E141.orphan", {"position": v(-120, 45) * mm});
            skPoint(sketch, "E142.orphan", {"position": v(-120, 105) * mm});
            skLineSegment(sketch, "E143", {"start": v(25, 39.5) * mm, "end": v(25, 34) * mm});
            skLineSegment(sketch, "E144", {"start": v(25, 34) * mm, "end": v(75, 34) * mm});
            skLineSegment(sketch, "E145", {"start": v(75, 39.5) * mm, "end": v(75, 34) * mm});
            skPoint(sketch, "E146.MirrorCS.end.orphan", {"position": v(75, 39.5) * mm});
            skPoint(sketch, "E146.MirrorCS.start.orphan", {"position": v(25, 39.5) * mm});
            skLineSegment(sketch, "E147", {"start": v(120, 39.5) * mm, "end": v(120, 34) * mm});
            skLineSegment(sketch, "E148", {"start": v(120, 34) * mm, "end": v(170, 34) * mm});
            skLineSegment(sketch, "E149", {"start": v(170, 34) * mm, "end": v(170, 39.5) * mm});
            skPoint(sketch, "E150.MirrorCS.end.orphan", {"position": v(170, 39.5) * mm});
            skLineSegment(sketch, "E151", {"start": v(25, -39.5) * mm, "end": v(25, -34) * mm});
            skLineSegment(sketch, "E152", {"start": v(25, -34) * mm, "end": v(75, -34) * mm});
            skLineSegment(sketch, "E153", {"start": v(75, -34) * mm, "end": v(75, -39.5) * mm});
            skLineSegment(sketch, "E154", {"start": v(120, -39.5) * mm, "end": v(120, -34) * mm});
            skLineSegment(sketch, "E155", {"start": v(120, -34) * mm, "end": v(170, -34) * mm});
            skLineSegment(sketch, "E156", {"start": v(170, -34) * mm, "end": v(170, -39.5) * mm});
            skLineSegment(sketch, "E157", {"start": v(280, 50.5) * mm, "end": v(280, 39.5) * mm});
            skLineSegment(sketch, "E158", {"start": v(280, 39.5) * mm, "end": v(330, 39.5) * mm});
            skLineSegment(sketch, "E159", {"start": v(330, 39.5) * mm, "end": v(330, 50.5) * mm});
            skLineSegment(sketch, "E160.trimOffspring", {"start": v(330, 50.5) * mm, "end": v(467.13, 50.5) * mm});
            skSolve(sketch);
        }
        {
            var Q0;
            Q0=makeQuery(id+"F7.imprint","IMPRINT",FACE,{"disambiguationData":[TD([[makeQuery(id+"F7.imprint","IMPRINT",EDGE,{"derivedFrom":sQuery(id+"F7.wireOp",EDGE,"E129.MirrorCS")}),1.0]])]});
            extrude(context, id + "F8", {"entities" : qUnion([Q0]), "depth" : 5.5 * mm, "offsetDistance" : 25 * mm});
        }
        {
            var Q0;
            Q0=makeQuery(id+"F5.imprint","IMPRINT",FACE,{"disambiguationData":[TD([[makeQuery(id+"F5.imprint","IMPRINT",EDGE,{"derivedFrom":sQuery(id+"F5.wireOp",EDGE,"E70.2")}),-1.0]])]});
            var sketch = newSketch(context, id + "F9", { "sketchPlane" : qUnion([Q0])});
            skLineSegment(sketch, "E161.0", {"start": v(210, 45) * mm, "end": v(210, -45) * mm});
            skLineSegment(sketch, "E162.0", {"start": v(210, -45) * mm, "end": v(342, -45) * mm});
            skLineSegment(sketch, "E163.0", {"start": v(210, 45) * mm, "end": v(342, 45) * mm});
            skLineSegment(sketch, "E164.0", {"start": v(510, -45) * mm, "end": v(510, 0) * mm});
            skLineSegment(sketch, "E165.0", {"start": v(510, 45) * mm, "end": v(510, 0) * mm});
            skLineSegment(sketch, "E166", {"start": v(342, -45) * mm, "end": v(342, 45) * mm, "construction": true});
            skLineSegment(sketch, "E167", {"start": v(510, 0) * mm, "end": v(210, 0) * mm, "construction": true});
            skLineSegment(sketch, "E168", {"start": v(510, 0) * mm, "end": v(580, 0) * mm, "construction": true});
            skLineSegment(sketch, "E169", {"start": v(580, 0) * mm, "end": v(580, 155) * mm});
            skLineSegment(sketch, "E170", {"start": v(510, 200.3) * mm, "end": v(342, 45) * mm});
            skLineSegment(sketch, "E171.MirrorCS", {"start": v(510, -200.3) * mm, "end": v(342, -45) * mm});
            skLineSegment(sketch, "E172.MirrorCS", {"start": v(580, 0) * mm, "end": v(580, -155) * mm});
            skLineSegment(sketch, "E173", {"start": v(510, -45) * mm, "end": v(510, -200.3) * mm});
            skLineSegment(sketch, "E174", {"start": v(510, 45) * mm, "end": v(510, 200.3) * mm});
            skLineSegment(sketch, "E175.bottom", {"start": v(362, -2.75) * mm, "end": v(402, -2.75) * mm});
            skLineSegment(sketch, "E175.top", {"start": v(362, 2.75) * mm, "end": v(402, 2.75) * mm});
            skLineSegment(sketch, "E175.left", {"start": v(362, -2.75) * mm, "end": v(362, 2.75) * mm});
            skLineSegment(sketch, "E175.right", {"start": v(402, -2.75) * mm, "end": v(402, 2.75) * mm});
            skPoint(sketch, "E175.middle", {"position": v(382, 0) * mm});
            skLineSegment(sketch, "E176.bottom", {"start": v(450, -2.75) * mm, "end": v(490, -2.75) * mm});
            skLineSegment(sketch, "E176.top", {"start": v(450, 2.75) * mm, "end": v(490, 2.75) * mm});
            skLineSegment(sketch, "E176.left", {"start": v(450, -2.75) * mm, "end": v(450, 2.75) * mm});
            skLineSegment(sketch, "E176.right", {"start": v(490, -2.75) * mm, "end": v(490, 2.75) * mm});
            skPoint(sketch, "E176.middle", {"position": v(470, 0) * mm});
            skPoint(sketch, "E177.orphan", {"position": v(210, -450) * mm});
            skPoint(sketch, "E178.orphan", {"position": v(210, 450) * mm});
            skLineSegment(sketch, "E179", {"start": v(580, -155) * mm, "end": v(510, -200.3) * mm});
            skPoint(sketch, "E179.startSnap0", {"position": v(461, -155) * mm});
            skLineSegment(sketch, "E180.MirrorCS", {"start": v(580, 155) * mm, "end": v(510, 200.3) * mm});
            skPoint(sketch, "E181.orphan", {"position": v(580, 265) * mm});
            skPoint(sketch, "E182.orphan", {"position": v(580, -265) * mm});
            skSolve(sketch);
        }
        {
            var Q0;
            {var subQ1=sQuery(id+"F9.wireOp",EDGE,"E164.0");Q0=makeQuery(id+"F9.imprint","IMPRINT",FACE,{"disambiguationData":[TD([[makeQuery(id+"F9.imprint","IMPRINT",EDGE,{"derivedFrom":subQ1}),-1.0]])]});}
            var Q1;
            {var subQ3=sQuery(id+"F9.wireOp",EDGE,"E173");Q1=makeQuery(id+"F9.imprint","IMPRINT",FACE,{"disambiguationData":[TD([[makeQuery(id+"F9.imprint","IMPRINT",EDGE,{"derivedFrom":subQ3}),-1.0]])]});}
            var Q2;
            {var subQ3=sQuery(id+"F9.wireOp",EDGE,"E162.0");Q2=makeQuery(id+"F9.imprint","IMPRINT",FACE,{"disambiguationData":[TD([[makeQuery(id+"F9.imprint","IMPRINT",EDGE,{"derivedFrom":subQ3}),1.0]])]});}
            var Q3;
            {var subQ3=sQuery(id+"F9.wireOp",EDGE,"E174");Q3=makeQuery(id+"F9.imprint","IMPRINT",FACE,{"disambiguationData":[TD([[makeQuery(id+"F9.imprint","IMPRINT",EDGE,{"derivedFrom":subQ3}),1.0]])]});}
            extrude(context, id + "F10", {"entities" : qUnion([Q0, Q1, Q2, Q3]), "depth" : 5.5 * mm, "offsetDistance" : 25 * mm});
        }
        {
            var Q0;
            Q0=makeQuery(id+"F10.opExtrude","CAP_FACE",FACE,{"disambiguationData":[OSD([sQuery(id+"F9.wireOp",EDGE,"E162.0"),sQuery(id+"F9.wireOp",EDGE,"E163.0"),sQuery(id+"F9.wireOp",EDGE,"E169"),sQuery(id+"F9.wireOp",EDGE,"E170"),sQuery(id+"F9.wireOp",EDGE,"E171.MirrorCS"),sQuery(id+"F9.wireOp",EDGE,"E172.MirrorCS"),sQuery(id+"F9.wireOp",EDGE,"E161.0"),sQuery(id+"F9.wireOp",EDGE,"E175.bottom"),sQuery(id+"F9.wireOp",EDGE,"E175.top"),sQuery(id+"F9.wireOp",EDGE,"E175.left"),sQuery(id+"F9.wireOp",EDGE,"E175.right"),sQuery(id+"F9.wireOp",EDGE,"E176.bottom"),sQuery(id+"F9.wireOp",EDGE,"E176.top"),sQuery(id+"F9.wireOp",EDGE,"E176.left"),sQuery(id+"F9.wireOp",EDGE,"E176.right")])],"isStart":false});
            var sketch = newSketch(context, id + "F11", { "sketchPlane" : qUnion([Q0])});
            skLineSegment(sketch, "E183.0", {"start": v(342, -2.75) * mm, "end": v(342, 2.75) * mm});
            skLineSegment(sketch, "E184.0", {"start": v(362, -2.75) * mm, "end": v(402, -2.75) * mm});
            skLineSegment(sketch, "E185.0", {"start": v(362, 2.75) * mm, "end": v(402, 2.75) * mm});
            skLineSegment(sketch, "E186.0", {"start": v(362, -2.75) * mm, "end": v(362, 2.75) * mm});
            skLineSegment(sketch, "E187.0", {"start": v(402, -2.75) * mm, "end": v(402, 2.75) * mm});
            skLineSegment(sketch, "E188.0", {"start": v(510, -2.75) * mm, "end": v(510, 0) * mm});
            skLineSegment(sketch, "E189.0", {"start": v(510, 2.75) * mm, "end": v(510, 0) * mm});
            skLineSegment(sketch, "E190.0", {"start": v(450, -2.75) * mm, "end": v(490, -2.75) * mm});
            skLineSegment(sketch, "E191.0", {"start": v(450, 2.75) * mm, "end": v(490, 2.75) * mm});
            skLineSegment(sketch, "E192.0", {"start": v(490, -2.75) * mm, "end": v(490, 2.75) * mm});
            skLineSegment(sketch, "E193.0", {"start": v(450, -2.75) * mm, "end": v(450, 2.75) * mm});
            skLineSegment(sketch, "E194", {"start": v(342, -2.75) * mm, "end": v(510, -2.75) * mm});
            skLineSegment(sketch, "E195", {"start": v(510, -2.75) * mm, "end": v(510, 2.75) * mm});
            skLineSegment(sketch, "E196", {"start": v(510, 2.75) * mm, "end": v(342, 2.75) * mm});
            skLineSegment(sketch, "E197", {"start": v(342, 2.75) * mm, "end": v(342, -2.75) * mm});
            skPoint(sketch, "E198.orphan", {"position": v(510, -45) * mm});
            skPoint(sketch, "E199.orphan", {"position": v(510, 45) * mm});
            skPoint(sketch, "E200.orphan", {"position": v(342, 45) * mm});
            skPoint(sketch, "E201.orphan", {"position": v(342, -45) * mm});
            skLineSegment(sketch, "E202", {"start": v(510, 2.75) * mm, "end": v(580, 2.75) * mm});
            skLineSegment(sketch, "E203", {"start": v(580, 2.75) * mm, "end": v(580, -2.75) * mm});
            skLineSegment(sketch, "E204", {"start": v(580, -2.75) * mm, "end": v(510, -2.75) * mm});
            skSolve(sketch);
        }
        {
            var Q0;
            {var subQ0=sQuery(id+"F11.wireOp",EDGE,"E192.0");Q0=makeQuery(id+"F11.imprint","IMPRINT",FACE,{"disambiguationData":[TD([[makeQuery(id+"F11.imprint","IMPRINT",EDGE,{"derivedFrom":subQ0}),-1.0]])]});}
            var Q1;
            Q1=makeQuery(id+"F11.imprint","IMPRINT",FACE,{"disambiguationData":[TD([[makeQuery(id+"F11.imprint","IMPRINT",EDGE,{"derivedFrom":sQuery(id+"F11.wireOp",EDGE,"E195")}),-1.0]])]});
            var Q2;
            {var subQ0=sQuery(id+"F11.wireOp",EDGE,"E192.0");Q2=makeQuery(id+"F11.imprint","IMPRINT",FACE,{"disambiguationData":[TD([[makeQuery(id+"F11.imprint","IMPRINT",EDGE,{"derivedFrom":subQ0}),1.0]])]});}
            var Q3;
            {var subQ0=sQuery(id+"F11.wireOp",EDGE,"E187.0");Q3=makeQuery(id+"F11.imprint","IMPRINT",FACE,{"disambiguationData":[TD([[makeQuery(id+"F11.imprint","IMPRINT",EDGE,{"derivedFrom":subQ0}),-1.0]])]});}
            var Q4;
            {var subQ0=sQuery(id+"F11.wireOp",EDGE,"E186.0");Q4=makeQuery(id+"F11.imprint","IMPRINT",FACE,{"disambiguationData":[TD([[makeQuery(id+"F11.imprint","IMPRINT",EDGE,{"derivedFrom":subQ0}),-1.0]])]});}
            var Q5;
            {var subQ0=sQuery(id+"F11.wireOp",EDGE,"E186.0");Q5=makeQuery(id+"F11.imprint","IMPRINT",FACE,{"disambiguationData":[TD([[makeQuery(id+"F11.imprint","IMPRINT",EDGE,{"derivedFrom":subQ0}),1.0]])]});}
            extrude(context, id + "F12", {"entities" : qUnion([Q0, Q1, Q2, Q3, Q4, Q5]), "depth" : 125 * mm, "offsetDistance" : 25 * mm});
        }
        {
            var Q0;
            Q0=makeQuery(id+"F9.imprint","IMPRINT",FACE,{"disambiguationData":[TD([[makeQuery(id+"F9.imprint","IMPRINT",EDGE,{"derivedFrom":sQuery(id+"F9.wireOp",EDGE,"E176.bottom")}),1.0]])]});
            var Q1;
            Q1=makeQuery(id+"F9.imprint","IMPRINT",FACE,{"disambiguationData":[TD([[makeQuery(id+"F9.imprint","IMPRINT",EDGE,{"derivedFrom":sQuery(id+"F9.wireOp",EDGE,"E175.bottom")}),1.0]])]});
            extrude(context, id + "F13", {"entities" : qUnion([Q0, Q1]), "operationType" : NewBodyOperationType.ADD, "depth" : 5.5 * mm, "offsetDistance" : 25 * mm});
        }
        {
            var Q0;
            Q0=makeQuery(id+"F13.boolean.opBoolean","MERGE",FACE,{"derivedFrom":[makeQuery(id+"F12.opExtrude","SWEPT_FACE",FACE,{"disambiguationData":[OSD([sQuery(id+"F11.wireOp",EDGE,"E196"),sQuery(id+"F11.wireOp",EDGE,"E202")])]}),makeQuery(id+"F13.opExtrude","SWEPT_FACE",FACE,{"disambiguationData":[OSD([sQuery(id+"F9.wireOp",EDGE,"E175.top")])]}),makeQuery(id+"F13.opExtrude","SWEPT_FACE",FACE,{"disambiguationData":[OSD([sQuery(id+"F9.wireOp",EDGE,"E176.top")])]})]});
            var sketch = newSketch(context, id + "F14", { "sketchPlane" : qUnion([Q0])});
            skPoint(sketch, "E205.0", {"position": v(-510, 0) * mm});
            skLineSegment(sketch, "E206", {"start": v(-510, 5.5) * mm, "end": v(-580, 35.5) * mm});
            skLineSegment(sketch, "E207", {"start": v(-580, 35.5) * mm, "end": v(-580, 100.5) * mm});
            skLineSegment(sketch, "E208", {"start": v(-580, 100.5) * mm, "end": v(-510, 130.5) * mm});
            skLineSegment(sketch, "E209", {"start": v(-510, 130.5) * mm, "end": v(-480, 130.5) * mm});
            skLineSegment(sketch, "E210", {"start": v(-480, 130.5) * mm, "end": v(-342, 5.5) * mm});
            skLineSegment(sketch, "E211", {"start": v(-510, 5.5) * mm, "end": v(-510, 130.5) * mm});
            skSolve(sketch);
        }
        {
            var Q0;
            {var subQ0=sQuery(id+"F14.wireOp",EDGE,"E208");Q0=makeQuery(id+"F14.imprint","IMPRINT",FACE,{"disambiguationData":[TD([[makeQuery(id+"F14.imprint","IMPRINT",EDGE,{"derivedFrom":subQ0}),1.0]])]});}
            var Q1;
            {var subQ0=sQuery(id+"F14.wireOp",EDGE,"E206");Q1=makeQuery(id+"F14.imprint","IMPRINT",FACE,{"disambiguationData":[TD([[makeQuery(id+"F14.imprint","IMPRINT",EDGE,{"derivedFrom":subQ0}),1.0]])]});}
            var Q2;
            {var subQ0=sQuery(id+"F14.wireOp",EDGE,"E210");Q2=makeQuery(id+"F14.imprint","IMPRINT",FACE,{"disambiguationData":[TD([[makeQuery(id+"F14.imprint","IMPRINT",EDGE,{"derivedFrom":subQ0}),1.0]])]});}
            extrude(context, id + "F15", {"entities" : qUnion([Q0, Q1, Q2]), "operationType" : NewBodyOperationType.REMOVE, "endBound" : BoundingType.UP_TO_NEXT, "oppositeDirection" : true, "depth" : 25 * mm, "offsetDistance" : 25 * mm});
        }
        {
            var Q0;
            Q0=makeQuery(id+"F6.opExtrude","CAP_FACE",FACE,{"disambiguationData":[OSD([sQuery(id+"F5.wireOp",EDGE,"E72"),sQuery(id+"F5.wireOp",EDGE,"E73"),sQuery(id+"F5.wireOp",EDGE,"E74"),sQuery(id+"F5.wireOp",EDGE,"E75"),sQuery(id+"F5.wireOp",EDGE,"E77"),sQuery(id+"F5.wireOp",EDGE,"E79.MirrorCS"),sQuery(id+"F5.wireOp",EDGE,"E80.MirrorCS"),sQuery(id+"F5.wireOp",EDGE,"E81.MirrorCS"),sQuery(id+"F5.wireOp",EDGE,"E82.MirrorCS")])],"isStart":false});
            var sketch = newSketch(context, id + "F16", { "sketchPlane" : qUnion([Q0])});
            skLineSegment(sketch, "E212.0", {"start": v(25, 34) * mm, "end": v(75, 34) * mm, "construction": true});
            skLineSegment(sketch, "E212.1", {"start": v(120, -34) * mm, "end": v(170, -34) * mm, "construction": true});
            skLineSegment(sketch, "E212.2", {"start": v(25, 45) * mm, "end": v(-120, 45) * mm, "construction": true});
            skLineSegment(sketch, "E212.3", {"start": v(25, 34) * mm, "end": v(25, 45) * mm, "construction": true});
            skLineSegment(sketch, "E212.5", {"start": v(75, 34) * mm, "end": v(75, 45) * mm, "construction": true});
            skLineSegment(sketch, "E212.6", {"start": v(25, -45) * mm, "end": v(-120, -45) * mm, "construction": true});
            skLineSegment(sketch, "E212.7", {"start": v(210, 45) * mm, "end": v(170, 45) * mm, "construction": true});
            skLineSegment(sketch, "E212.10", {"start": v(120, -45) * mm, "end": v(75, -45) * mm, "construction": true});
            skLineSegment(sketch, "E212.11", {"start": v(120, 45) * mm, "end": v(75, 45) * mm, "construction": true});
            skLineSegment(sketch, "E212.12", {"start": v(210, 45) * mm, "end": v(510, 45) * mm, "construction": true});
            skLineSegment(sketch, "E212.13", {"start": v(120, 34) * mm, "end": v(170, 34) * mm, "construction": true});
            skLineSegment(sketch, "E212.14", {"start": v(120, 34) * mm, "end": v(120, 45) * mm, "construction": true});
            skLineSegment(sketch, "E212.15", {"start": v(25, -34) * mm, "end": v(75, -34) * mm, "construction": true});
            skLineSegment(sketch, "E212.16", {"start": v(210, -45) * mm, "end": v(510, -45) * mm, "construction": true});
            skLineSegment(sketch, "E212.17", {"start": v(170, 34) * mm, "end": v(170, 45) * mm, "construction": true});
            skLineSegment(sketch, "E212.18", {"start": v(210, -45) * mm, "end": v(170, -45) * mm, "construction": true});
            skLineSegment(sketch, "E212.19", {"start": v(25, -34) * mm, "end": v(25, -45) * mm, "construction": true});
            skLineSegment(sketch, "E212.20", {"start": v(75, -34) * mm, "end": v(75, -45) * mm, "construction": true});
            skLineSegment(sketch, "E212.21", {"start": v(120, -34) * mm, "end": v(120, -45) * mm, "construction": true});
            skLineSegment(sketch, "E212.22", {"start": v(170, -45) * mm, "end": v(170, -34) * mm, "construction": true});
            skLineSegment(sketch, "E213", {"start": v(-120, -39.5) * mm, "end": v(518, -39.5) * mm});
            skLineSegment(sketch, "E214", {"start": v(518, -39.5) * mm, "end": v(518, 0) * mm});
            skLineSegment(sketch, "E215", {"start": v(-120, -39.5) * mm, "end": v(-120, 0) * mm});
            skLineSegment(sketch, "E216", {"start": v(-120, 0) * mm, "end": v(518, 0) * mm, "construction": true});
            skLineSegment(sketch, "E217.MirrorCS", {"start": v(518, 39.5) * mm, "end": v(518, 0) * mm});
            skLineSegment(sketch, "E218.MirrorCS", {"start": v(-120, 39.5) * mm, "end": v(518, 39.5) * mm});
            skLineSegment(sketch, "E219.MirrorCS", {"start": v(-120, 39.5) * mm, "end": v(-120, 0) * mm});
            skLineSegment(sketch, "E220", {"start": v(280, -39.5) * mm, "end": v(280, 39.5) * mm});
            skSolve(sketch);
        }
        {
            var Q0;
            {var subQ6=sQuery(id+"F16.wireOp",EDGE,"E214");Q0=makeQuery(id+"F16.imprint","IMPRINT",FACE,{"disambiguationData":[TD([[makeQuery(id+"F16.imprint","IMPRINT",EDGE,{"derivedFrom":subQ6}),1.0]])]});}
            var Q1;
            {var subQ0=sQuery(id+"F16.wireOp",EDGE,"E220");Q1=makeQuery(id+"F16.imprint","IMPRINT",FACE,{"disambiguationData":[TD([[makeQuery(id+"F16.imprint","IMPRINT",EDGE,{"derivedFrom":subQ0}),-1.0]])]});}
            var Q2;
            {var subQ4=sQuery(id+"F16.wireOp",EDGE,"E215");Q2=makeQuery(id+"F16.imprint","IMPRINT",FACE,{"disambiguationData":[TD([[makeQuery(id+"F16.imprint","IMPRINT",EDGE,{"derivedFrom":subQ4}),1.0]])]});}
            var Q3;
            {var subQ0=makeQuery(id+"F6.opExtrude","CAP_EDGE",EDGE,{"disambiguationData":[OSD([sQuery(id+"F5.wireOp",EDGE,"E105")])],"isStart":false});Q3=makeQuery(id+"F16.imprint","IMPRINT",FACE,{"disambiguationData":[TD([[makeQuery(id+"F16.imprint","IMPRINT",EDGE,{"derivedFrom":subQ0}),-1.0]])]});}
            var Q4;
            {var subQ4=makeQuery(id+"F6.opExtrude","CAP_EDGE",EDGE,{"disambiguationData":[OSD([sQuery(id+"F5.wireOp",EDGE,"E105")])],"isStart":false});Q4=makeQuery(id+"F16.imprint","IMPRINT",FACE,{"disambiguationData":[TD([[makeQuery(id+"F16.imprint","IMPRINT",EDGE,{"derivedFrom":subQ4}),1.0]])]});}
            extrude(context, id + "F17", {"entities" : qUnion([Q0, Q1, Q2, Q3, Q4]), "depth" : 5.5 * mm, "offsetDistance" : 25 * mm});
        }
    });
